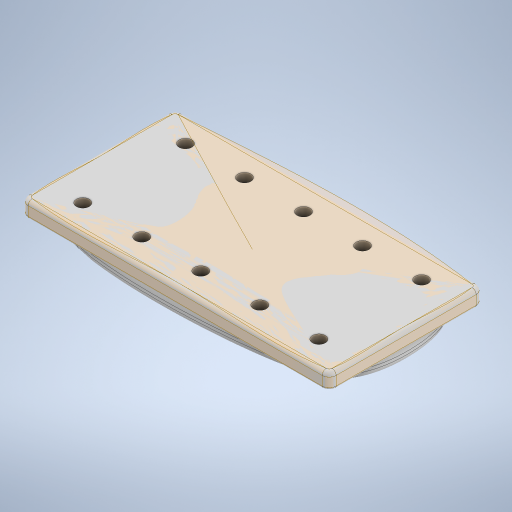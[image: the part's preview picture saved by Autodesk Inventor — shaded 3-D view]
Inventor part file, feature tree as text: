
AUTODESK INVENTOR PART (.ipt)
format: ipt  version: 2024.1 (Build 281209000, 209)  size: 959,488 bytes
history: native  units: mm
features: other x27, fillet x4, sketch x3, extrude x3, plane x1, mirror x1
ambient origin geometry x8: Origin, YZ Plane, XZ Plane, XY Plane, X Axis, Y Axis, Z Axis, Center Point
bodies: Solid1 (feature_tree)
feature tree (39):
  sketch  "Sketch1"  dims[d1=30.0mm d2=3.0mm d3=0.0mm d9=60.0mm]
  extrude  "Extrusion1"  Depth=3.0mm TaperAngle=0.0deg
  fillet  "Fillet1"  Radius=60.0mm
  plane  "Work Plane1"
  extrude  "Extrusion5"  Depth=1.36mm
  fillet  "Fillet2"  Radius=3.0mm
  fillet  "Fillet3"  Radius=0.4mm
  fillet  "Fillet4"  Radius=0.8mm
  extrude  "Extrusion6"  Depth=5.0mm
  other  "Form1"
  mirror  "Mirror1"
  sketch  "Sketch5"  dims[d10=1.225mm d13=1.36mm d14=3.0mm d15=0.0mm d16=0.4mm d17=0.8mm]
  sketch  "Sketch6"  dims[d18=5.0mm d19=5.0mm d20=7.0mm d21=7.0mm d22=11.5mm d23=11.5mm d24=11.5mm d25=11.5mm d26=2.5mm d27=3.0mm d28=0.0mm]
  other  "biscuit"
  other  "Srf1"
  other  "Srf2"
  other  "Srf3"
  other  "Srf4"
  other  "Srf5"
  other  "Srf6"
  other  "Srf7"
  other  "Srf8"
  other  "Srf9"
  other  "Srf10"
  other  "Srf11"
  other  "Srf12"
  other  "Srf13"
  other  "Srf14"
  other  "Srf15"
  other  "Srf16"
  other  "Srf17"
  other  "Srf18"
  other  "Srf19"
  other  "Srf20"
  other  "Srf21"
  other  "Srf22"
  other  "Srf23"
  other  "Srf24"
  other  "Srf25"
